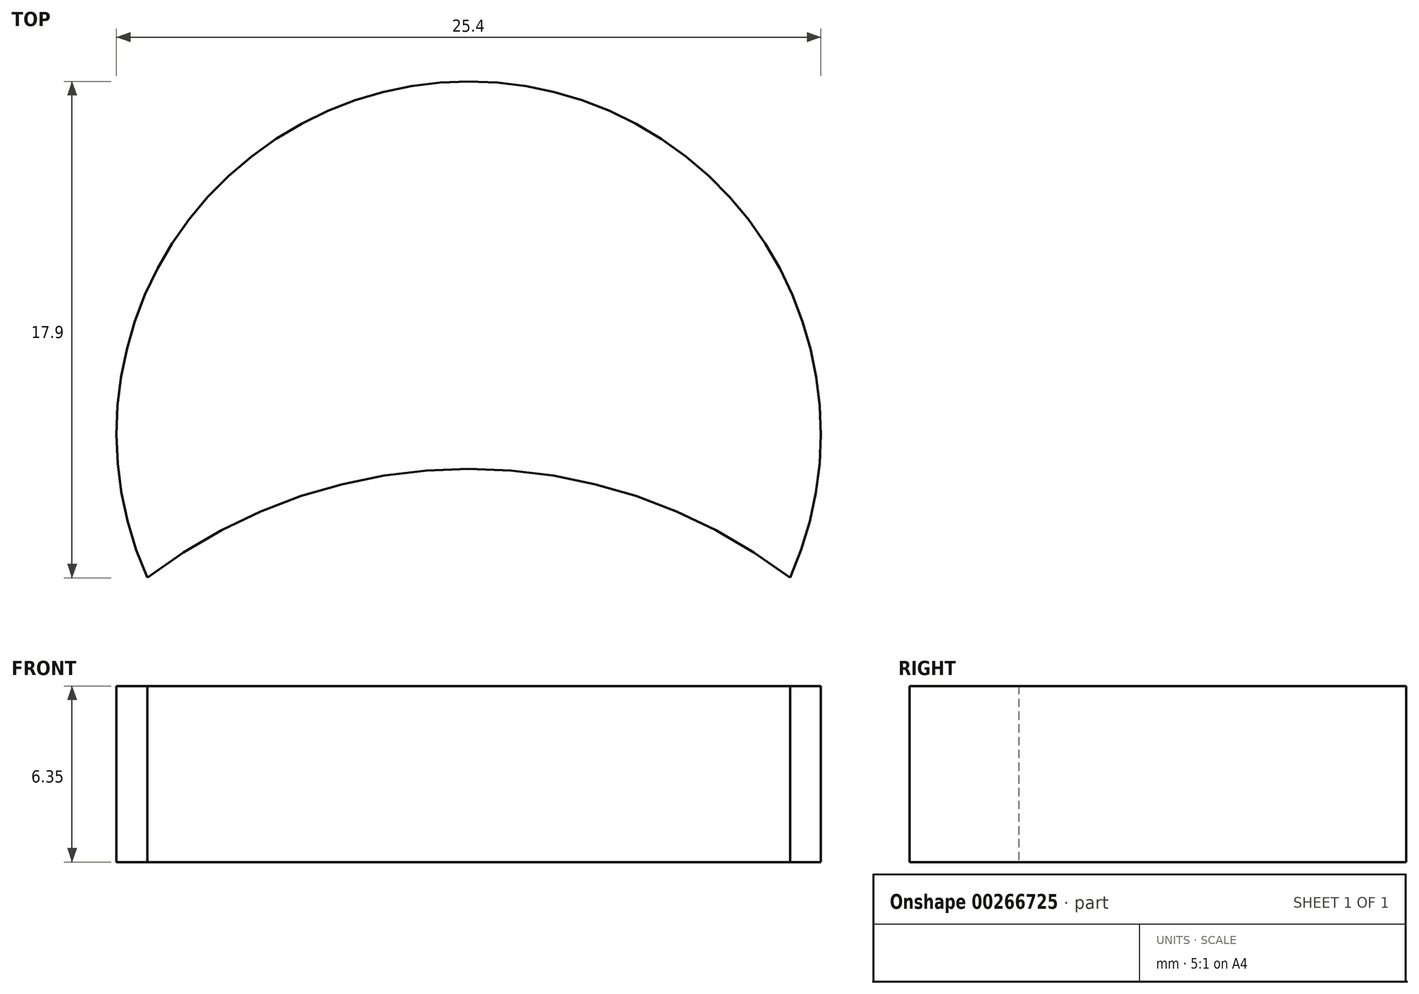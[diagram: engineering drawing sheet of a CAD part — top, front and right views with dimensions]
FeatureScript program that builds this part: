
annotation { "Feature Type Name" : "Feature", "Feature Type Description" : "" }
export const myFeature = defineFeature(function(context is Context, id is Id, definition is map)
    precondition{}
    {
        {
            var Q0;
            Q0=qCreatedBy(makeId("Top.planeOp"),FACE);
            var sketch = newSketch(context, id + "F0", { "sketchPlane" : qUnion([Q0])});
            skCircle(sketch, "E0", {"center": v(0, 0) * mm, "radius": 12.7 * mm});
            skCircle(sketch, "E1", {"center": v(0, -20.32) * mm, "radius": 19.05 * mm});
            skSolve(sketch);
        }
        {
            var Q0;
            {var subQ0=sQuery(id+"F0.wireOp",EDGE,"E1");var subQ1=sQuery(id+"F0.wireOp",EDGE,"E0");var subQ2=makeQuery(id+"F0.imprint","INTERSECT",VERTEX,{"disambiguationData":[OD(0.0)],"derivedFrom":[subQ1,subQ0]});Q0=makeQuery(id+"F0.imprint","IMPRINT",FACE,{"disambiguationData":[TD([[makeQuery(id+"F0.imprint","IMPRINT",EDGE,{"disambiguationData":[TD([[subQ2,1.0]])],"derivedFrom":subQ1}),1.0]])]});}
            extrude(context, id + "F1", {"entities" : qUnion([Q0]), "depth" : 6.35 * mm});
        }
    });
